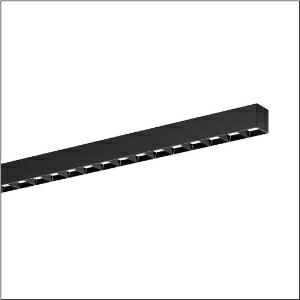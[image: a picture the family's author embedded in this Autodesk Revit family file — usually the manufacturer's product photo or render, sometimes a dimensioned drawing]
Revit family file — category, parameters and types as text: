
# Revit family: silica_r__21_51mx21tat4b_6284
name_source: partatom
category: Lighting Fixtures
units: mm (PartAtom-declared; Revit-internal decimal feet)

## family parameters
Cut with Voids When Loaded = No
Host = Face
Light Source = No
Part Type = Normal
Room Calculation Point = No
Round Connector Dimension = Use Diameter
Shared = No

## types (1)
- --- (1 x LED, 3720 lm, 32.2 W, 6500K)
    Apparent Load = 32 VA
    CIE Flux Codes = 85 99 100 100 100
    Color Rendering = 80
    Color Temperature = 6500K
    Default Elevation = 1800 mm
    Description = Silica® 21, office luminaire, primary light control with darklight reflector, of PMMA, black, CAT 2 (L<= 3000cd/m²), light emission: direct distribution, primary light characteristic: symmetric, installation type: surface-mounted, LED, rated luminous flux: 3.720lm, luminous efficacy: 110lm/W, light colour: 8tw, colour temperature: 2700..6500K, control gear: ECG DALI, with terminal, 3+2-pole, max. 2.5mm², mains connection: 220..240V, AC, 50/60Hz, rated input power: 33.8W, luminaire housing, of aluminium, jet black (RAL 9005), length: 1.204mm, width: 53mm, height: 53mm, protection rating (complete): IP20, insulation class (complete): insulation class I (protective earthing), certification: CE, permissible operating ambient temperature: 0..+35°C, standard: EN 50419, packaging unit: 1 piece
    Height = 0 mm  [stored 0 ft]
    Lamp = 1 x LED
    Lamp Light Flux = 3720 lm
    Lamp Power = 32.2 W
    Lamp count = 1
    Length = 1204 mm
    Luminous efficacy = 116 lm/W
    Manufacturer = Siteco
    ModVariant = No
    Model = 51MX21TAT4B
    Mounting Place = Ceiling
    Mounting Type = Recessed
    Number of Poles = 1
    OnlyDefault = Yes
    Power Factor = 1
    Product Name = Silica® 21
    Product group = office luminaire | ceiling recessed
    ProductGroupID = 401
    Protection Class = Protection class I
    Protection Degree = IP 20
    RLX_Detail_Level = 1
    RLX_Emergency_Light_Flux = 0 lm
    RLX_Emergency_Type = 0
    RLX_Emergency_Type_DB = No
    RlxData = <blob elided: 40321 chars, md5=4353e420>
    Socket = socket
    Standby Power = 0 W
    System Light Flux = 3720 lm
    System Power = 32 W
    Type Comments = individual setting
    Type Image = l_1313577.jpg
    URL = http://relux.com
    VarID = @adj_089439
    Voltage = 0 V
    Weight = 0.00 kg
    Width = 53 mm

note: [stored X ft] marks values corroborated as IEEE doubles in the binary element streams (Revit-internal decimal feet)

## geometry (parser evidence)
native form markers: Blend x4, Sweep x9
no freeform markers — native parametric forms only
